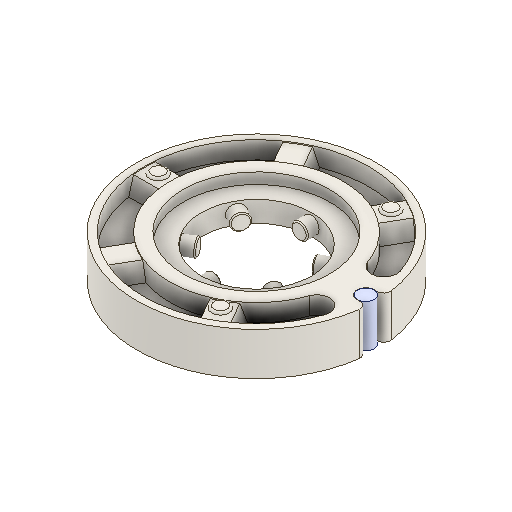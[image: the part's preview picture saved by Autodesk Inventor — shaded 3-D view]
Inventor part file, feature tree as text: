
AUTODESK INVENTOR PART (.ipt)
format: ipt  version: 2022 (Build 260153000, 153)  size: 294,912 bytes
history: native  units: mm
features: other x1, mirror x1
ambient origin geometry x8: Origin, YZ Plane, XZ Plane, XY Plane, X Axis, Y Axis, Z Axis, Center Point
bodies: Volumenkörper1 (feature_tree), Volumenkörper2 (feature_tree)
feature tree (2):
  other  "Boss-Extrude4"
  mirror  "Mirror1"
